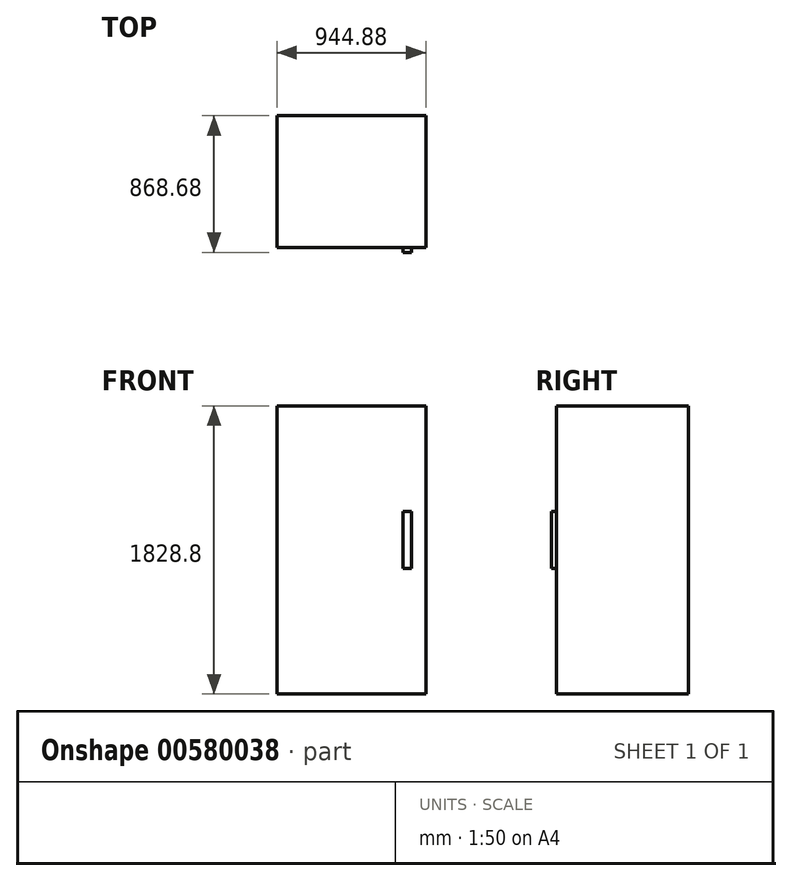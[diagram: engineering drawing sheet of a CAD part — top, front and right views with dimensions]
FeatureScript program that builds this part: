
annotation { "Feature Type Name" : "Feature", "Feature Type Description" : "" }
export const myFeature = defineFeature(function(context is Context, id is Id, definition is map)
    precondition{}
    {
        {
            var Q0;
            Q0=qCreatedBy(makeId("Top.planeOp"),FACE);
            var sketch = newSketch(context, id + "F0", { "sketchPlane" : qUnion([Q0])});
            skLineSegment(sketch, "E0.bottom", {"start": v(-466.96, 550.74) * mm, "end": v(477.92, 550.74) * mm});
            skLineSegment(sketch, "E0.top", {"start": v(-466.96, -287.46) * mm, "end": v(477.92, -287.46) * mm});
            skLineSegment(sketch, "E0.left", {"start": v(-466.96, 550.74) * mm, "end": v(-466.96, -287.46) * mm});
            skLineSegment(sketch, "E0.right", {"start": v(477.92, 550.74) * mm, "end": v(477.92, -287.46) * mm});
            skSolve(sketch);
        }
        {
            var Q0;
            Q0 = qSketchRegion(id + "F0", true);
            extrude(context, id + "F1", {"entities" : qUnion([Q0]), "depth" : 1828.8 * mm, "offsetDistance" : 30.48 * mm});
        }
        {
            var Q0;
            Q0=makeQuery(id+"F1.opExtrude","SWEPT_FACE",FACE,{"disambiguationData":[OSD([sQuery(id+"F0.wireOp",EDGE,"E0.top")])]});
            var sketch = newSketch(context, id + "F2", { "sketchPlane" : qUnion([Q0])});
            skLineSegment(sketch, "E1.bottom", {"start": v(333.65, 1159.84) * mm, "end": v(387.74, 1159.84) * mm});
            skLineSegment(sketch, "E1.top", {"start": v(333.65, 795.6) * mm, "end": v(387.74, 795.6) * mm});
            skLineSegment(sketch, "E1.left", {"start": v(333.65, 1159.84) * mm, "end": v(333.65, 795.6) * mm});
            skLineSegment(sketch, "E1.right", {"start": v(387.74, 1159.84) * mm, "end": v(387.74, 795.6) * mm});
            skSolve(sketch);
        }
        {
            var Q0;
            Q0 = qSketchRegion(id + "F2", true);
            extrude(context, id + "F3", {"entities" : qUnion([Q0]), "operationType" : NewBodyOperationType.ADD, "depth" : 30.48 * mm, "offsetDistance" : 30.48 * mm});
        }
    });
